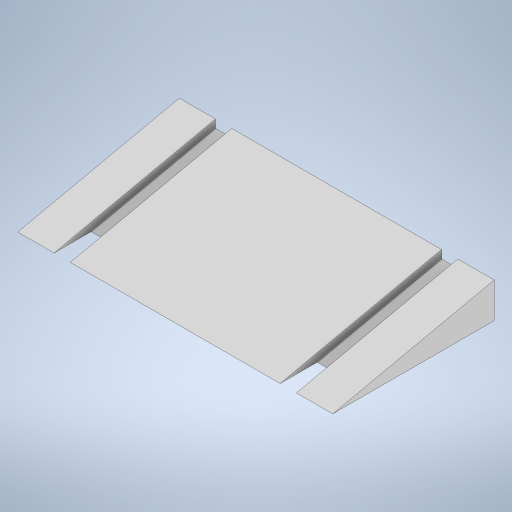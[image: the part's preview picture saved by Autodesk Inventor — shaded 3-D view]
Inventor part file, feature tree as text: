
AUTODESK INVENTOR PART (.ipt)
format: ipt  version: 2023.1 (Build 271208000, 208)  size: 258,048 bytes
history: native  units: mm
features: sketch x5, extrude x3, thread x2, sweep x1, mirror x1, projected_geometry x1
ambient origin geometry x8: Origin, YZ Plane, XZ Plane, XY Plane, X Axis, Y Axis, Z Axis, Center Point
bodies: 实体1 (feature_tree)
feature tree (13):
  extrude  "拉伸1"  Depth=550.0mm
  sweep  "扫掠1"
  mirror  "镜像1"
  extrude  "拉伸2"  Depth=45.0mm
  extrude  "拉伸3"  TaperAngle=0.0deg  [1 undecoded]
  thread  "螺纹1"  [1 undecoded]
  thread  "螺纹2"  [1 undecoded]
  sketch  "草图2"  dims[d0=120.0mm d1=550.0mm]
  sketch  "草图3"  dims[d2=200.0mm d3=390.0mm d4=0.0mm]
  sketch  "草图4"  dims[d5=20.0mm d6=45.0mm]
  sketch  "草图5"  dims[d8=10.0mm d9=0.0mm d10=0.0mm d11=60.0mm d12=30.0mm]
  sketch  "草图6"  dims[d13=15.0mm d14=0.0mm d15=30.0mm d16=12.0mm d17=12.0mm d18=20.0mm d19=25.0mm d20=15.0mm d21=0.0mm d22=15.0mm d23=0.0mm d24=15.0mm d25=0.0mm]
  projected_geometry  "投影回路1"
note: 3 required parameter values undecoded (feature->parameter linkage not recoverable at this tier; creation-order binding heuristic only, values carry confidence <= 0.55)
